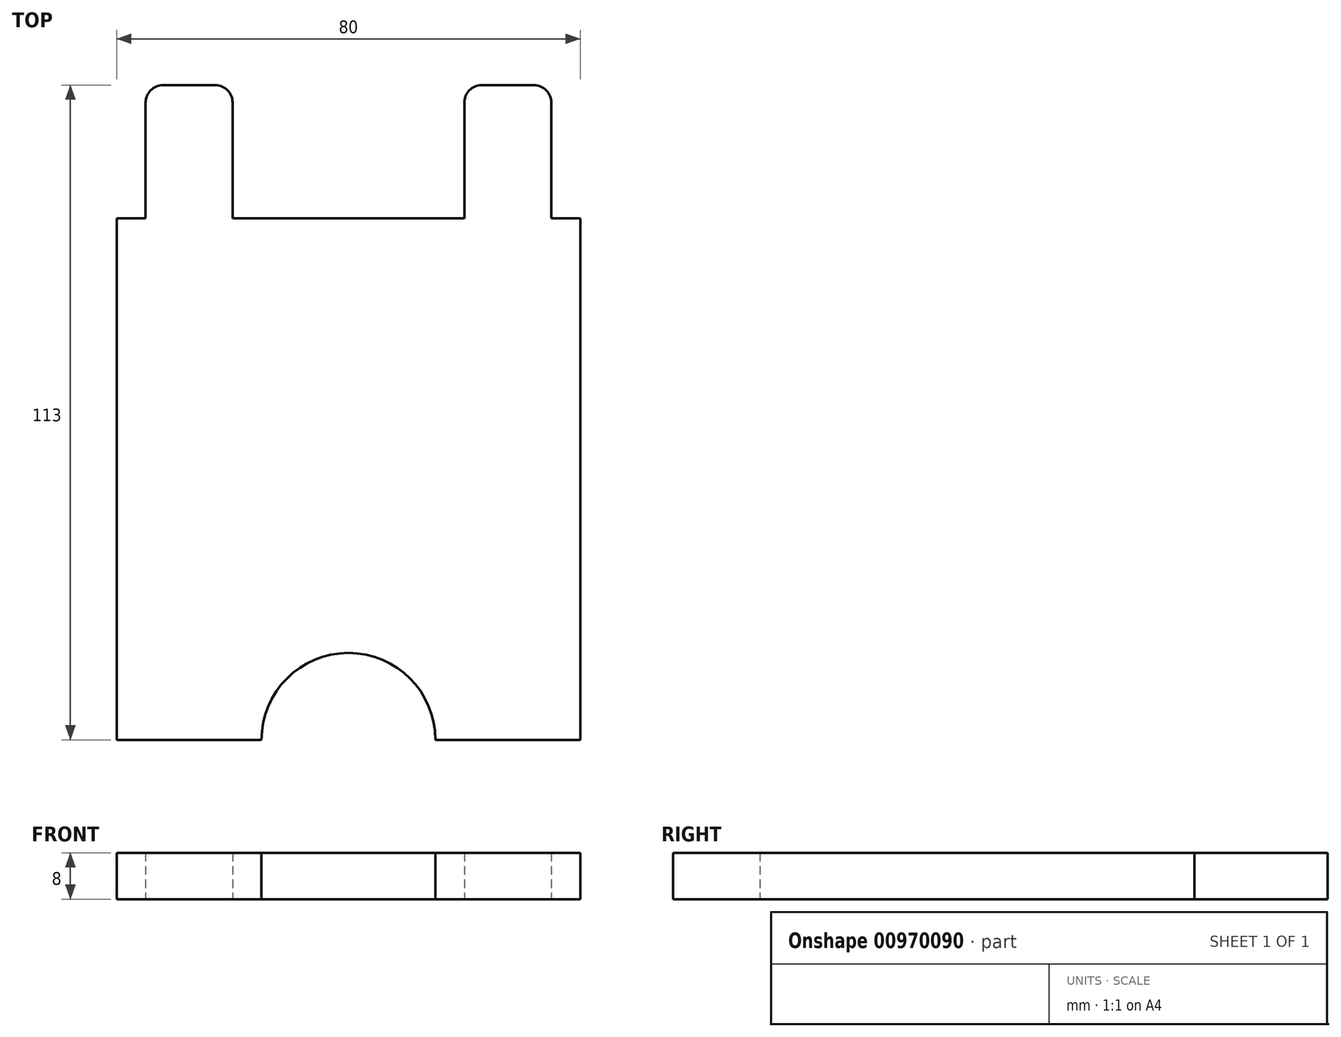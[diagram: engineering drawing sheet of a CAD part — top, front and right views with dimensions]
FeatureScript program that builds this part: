
annotation { "Feature Type Name" : "Feature", "Feature Type Description" : "" }
export const myFeature = defineFeature(function(context is Context, id is Id, definition is map)
    precondition{}
    {
        {
            var Q0;
            Q0=qCreatedBy(makeId("Top.planeOp"),FACE);
            var sketch = newSketch(context, id + "F0", { "sketchPlane" : qUnion([Q0])});
            skLineSegment(sketch, "E0.bottom", {"start": v(-39.22, -1.03) * mm, "end": v(-34.22, -1.03) * mm});
            skLineSegment(sketch, "E0.top", {"start": v(-39.22, -91.03) * mm, "end": v(-14.22, -91.03) * mm});
            skLineSegment(sketch, "E0.left", {"start": v(-39.22, -1.03) * mm, "end": v(-39.22, -91.03) * mm});
            skLineSegment(sketch, "E0.right", {"start": v(40.78, -1.03) * mm, "end": v(40.78, -91.03) * mm});
            skLineSegment(sketch, "E1.bottom", {"start": v(-19.22, -1.03) * mm, "end": v(-17.2, -1.03) * mm});
            skLineSegment(sketch, "E2.top", {"start": v(-31.22, 21.97) * mm, "end": v(-22.22, 21.97) * mm});
            skLineSegment(sketch, "E2.left", {"start": v(-34.22, -1.03) * mm, "end": v(-34.22, 18.97) * mm});
            skLineSegment(sketch, "E2.right", {"start": v(-19.22, -1.03) * mm, "end": v(-19.22, 18.97) * mm});
            skLineSegment(sketch, "E3.top", {"start": v(23.78, 21.97) * mm, "end": v(32.78, 21.97) * mm});
            skLineSegment(sketch, "E3.left", {"start": v(20.78, -1.03) * mm, "end": v(20.78, 18.97) * mm});
            skLineSegment(sketch, "E3.right", {"start": v(35.78, -1.03) * mm, "end": v(35.78, 18.97) * mm});
            skPoint(sketch, "E4.visualSharp", {"position": v(-34.22, 21.97) * mm});
            skArc(sketch, "E4.filletArc", {"start": v(-31.22, 21.97) * mm, "mid": v(-33.34, 21.09) * mm, "end": v(-34.22, 18.97) * mm});
            skPoint(sketch, "E5.visualSharp", {"position": v(-19.22, 21.97) * mm});
            skArc(sketch, "E5.filletArc", {"start": v(-19.22, 18.97) * mm, "mid": v(-20.1, 21.09) * mm, "end": v(-22.22, 21.97) * mm});
            skPoint(sketch, "E6.visualSharp", {"position": v(20.78, 21.97) * mm});
            skArc(sketch, "E6.filletArc", {"start": v(23.78, 21.97) * mm, "mid": v(21.66, 21.09) * mm, "end": v(20.78, 18.97) * mm});
            skPoint(sketch, "E7.visualSharp", {"position": v(35.78, 21.97) * mm});
            skArc(sketch, "E7.filletArc", {"start": v(35.78, 18.97) * mm, "mid": v(34.9, 21.09) * mm, "end": v(32.78, 21.97) * mm});
            skArc(sketch, "E8", {"start": v(-14.22, -91.03) * mm, "mid": v(0.78, -76.03) * mm, "end": v(15.78, -91.03) * mm});
            skLineSegment(sketch, "E9.trimOffspring", {"start": v(15.78, -91.03) * mm, "end": v(40.78, -91.03) * mm});
            skLineSegment(sketch, "E10.trimOffspring", {"start": v(35.78, -1.03) * mm, "end": v(40.78, -1.03) * mm});
            skPoint(sketch, "E11", {"position": v(-19.22, -1.03) * mm});
            skLineSegment(sketch, "E12.trimOffspring", {"start": v(-19.22, -1.03) * mm, "end": v(20.78, -1.03) * mm});
            skSolve(sketch);
        }
        {
            var Q0;
            Q0=makeQuery(id+"F0.imprint","IMPRINT",FACE,{"disambiguationData":[TD([[makeQuery(id+"F0.imprint","IMPRINT",EDGE,{"derivedFrom":sQuery(id+"F0.wireOp",EDGE,"E0.bottom")}),-1.0]])]});
            extrude(context, id + "F1", {"entities" : qUnion([Q0]), "depth" : 8 * mm, "offsetDistance" : 25 * mm});
        }
    });
